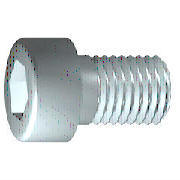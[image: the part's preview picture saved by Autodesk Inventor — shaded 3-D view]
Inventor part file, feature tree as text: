
AUTODESK INVENTOR PART (.ipt)
format: ipt  version: 2024.3 (Build 283343000, 343)  size: 193,024 bytes
history: native  units: mm (DEFAULTED — no unit token found)
features: extrude x1, plane x1, fillet x1
ambient origin geometry x7: Origin, YZ Plane, XY Plane, X Axis, Y Axis, Z Axis, Center Point
bodies: Solid1 (feature_tree), Body (feature_tree)
feature tree (3):
  extrude  "Slot"  Depth=17.5mm
  plane  "Work Plane1"
  fillet  "Fillet2"  Radius=0.61355mm
